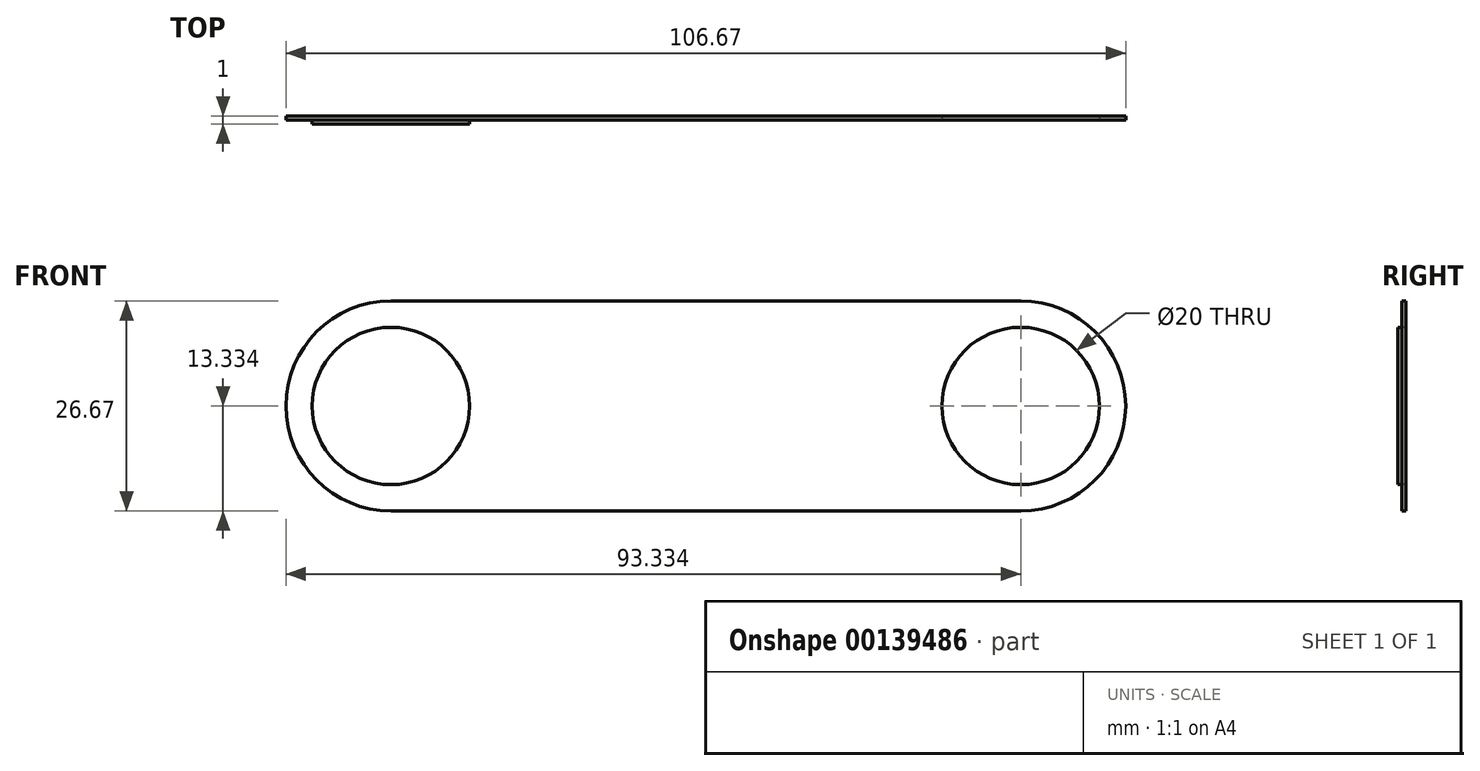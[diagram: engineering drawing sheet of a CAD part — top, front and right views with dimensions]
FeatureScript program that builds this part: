
annotation { "Feature Type Name" : "Feature", "Feature Type Description" : "" }
export const myFeature = defineFeature(function(context is Context, id is Id, definition is map)
    precondition{}
    {
        {
            assignVariable(context, id + "F0", {"name" : "depth", "anyValue" : .5});
        }
        {
            var Q0;
            Q0=qCreatedBy(makeId("Front.planeOp"),FACE);
            var sketch = newSketch(context, id + "F1", { "sketchPlane" : qUnion([Q0])});
            skLineSegment(sketch, "E0.bottom", {"start": v(-95.05, 45.4) * mm, "end": v(-15.05, 45.4) * mm});
            skLineSegment(sketch, "E0.top", {"start": v(-95.05, 18.74) * mm, "end": v(-15.05, 18.74) * mm});
            skArc(sketch, "E1", {"start": v(-15.05, 18.74) * mm, "mid": v(-1.71, 32.07) * mm, "end": v(-15.05, 45.4) * mm});
            skArc(sketch, "E2", {"start": v(-95.05, 45.4) * mm, "mid": v(-108.38, 32.07) * mm, "end": v(-95.05, 18.74) * mm});
            skSolve(sketch);
        }
        {
            var Q0;
            Q0=makeQuery(id+"F1.imprint","IMPRINT",FACE,{"disambiguationData":[TD([[makeQuery(id+"F1.imprint","IMPRINT",EDGE,{"derivedFrom":sQuery(id+"F1.wireOp",EDGE,"E0.bottom")}),-1.0]])]});
            extrude(context, id + "F2", {"entities" : qUnion([Q0]), "depth" : (getVariable(context, 'depth')) * mm});
        }
        {
            var Q0;
            Q0=makeQuery(id+"F2.opExtrude","CAP_FACE",FACE,{"disambiguationData":[OSD([sQuery(id+"F1.wireOp",EDGE,"E0.bottom"),sQuery(id+"F1.wireOp",EDGE,"E0.top"),sQuery(id+"F1.wireOp",EDGE,"E1"),sQuery(id+"F1.wireOp",EDGE,"E2")])],"isStart":false});
            var sketch = newSketch(context, id + "F3", { "sketchPlane" : qUnion([Q0])});
            skCircle(sketch, "E3", {"center": v(-95.05, 32.07) * mm, "radius": 10 * mm});
            skCircle(sketch, "E4", {"center": v(-15.05, 32.07) * mm, "radius": 10 * mm});
            skSolve(sketch);
        }
        {
            var Q0;
            Q0=makeQuery(id+"F3.imprint","IMPRINT",FACE,{"disambiguationData":[TD([[makeQuery(id+"F3.imprint","IMPRINT",EDGE,{"derivedFrom":sQuery(id+"F3.wireOp",EDGE,"E3")}),1.0]])]});
            var Q1;
            Q1=sQuery(id+"F3.wireOp",EDGE,"E3");
            extrude(context, id + "F4", {"entities" : qUnion([Q0]), "operationType" : NewBodyOperationType.ADD, "surfaceEntities" : qUnion([Q1]), "depth" : (getVariable(context, 'depth')) * mm});
        }
        {
            var Q0;
            Q0=makeQuery(id+"F3.imprint","IMPRINT",FACE,{"disambiguationData":[TD([[makeQuery(id+"F3.imprint","IMPRINT",EDGE,{"derivedFrom":sQuery(id+"F3.wireOp",EDGE,"E4")}),1.0]])]});
            var Q1;
            Q1=sQuery(id+"F3.wireOp",EDGE,"E4");
            extrude(context, id + "F5", {"entities" : qUnion([Q0]), "operationType" : NewBodyOperationType.REMOVE, "surfaceEntities" : qUnion([Q1]), "oppositeDirection" : true, "depth" : (getVariable(context, 'depth')) * mm});
        }
    });
